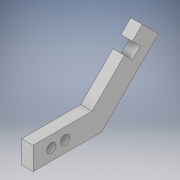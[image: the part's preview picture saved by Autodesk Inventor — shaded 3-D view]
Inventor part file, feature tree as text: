
AUTODESK INVENTOR PART (.ipt)
format: ipt  version: 2019 (Build 230136000, 136)  size: 113,664 bytes
history: native  units: in
note: dims shown in document units (in); Inventor stores cm internally (conversion verified against a paired STEP export)
features: extrude x1, sketch x1
ambient origin geometry x8: Origin, YZ Plane, XZ Plane, XY Plane, X Axis, Y Axis, Z Axis, Center Point
bodies: Solid1 (feature_tree)
feature tree (2):
  extrude  "Extrusion1"  Depth=0.125in
  sketch  "Sketch1"  dims[d0=0.1in d1=0.15in d2=0.1in d3=0.2in d4=0.25in d5=0.125in d6=135.0deg d11=0.125in d12=0.0in d14=0.125in d15=0.5in]
